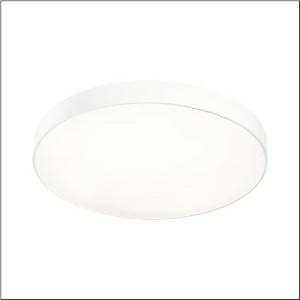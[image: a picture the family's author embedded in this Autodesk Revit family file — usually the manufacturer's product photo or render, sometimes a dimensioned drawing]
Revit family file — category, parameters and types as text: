
# Revit family: round_21_l_51mr38fd0421w
name_source: partatom
category: Lighting Fixtures
units: mm (PartAtom-declared; Revit-internal decimal feet)

## family parameters
Cut with Voids When Loaded = No
Host = Face
Light Source = No
Part Type = Normal
Room Calculation Point = No
Round Connector Dimension = Use Diameter
Shared = No

## types (1)
- Round 21 L (1 x LED, 14150 lm, 97 W, 4000K)
    Apparent Load = 97 VA
    CIE Flux Codes = 49 80 96 100 100
    Color Rendering = 80
    Color Temperature = 4000K
    Default Elevation = 1800 mm
    Description = Round 21 L, wall and ceiling luminaire, primary optical cover: cover, of PMMA, opal, light emission: direct distribution, primary light characteristic: symmetric, installation type: suspended mounting, surface-mounted, LED, rated luminous flux: 13.080lm, luminous efficacy: 146lm/W, light colour: 840, colour temperature: 4000K, control gear: DALI 2, with terminal, 5-pole, mains connection: 230V, AC, 50/60Hz, rated input power: 97W, housing, of aluminium, coated, white, diameter: 850mm, height: 62mm, protection rating (complete): IP40, insulation class (complete): insulation class I (protective earthing), certification: CE, impact resistance: IK04, permissible operating ambient temperature: -10..+35°C, packaging unit: 1 piece
    Height = 87 mm
    Lamp = 1 x LED
    Lamp Light Flux = 14150 lm
    Lamp Power = 97 W
    Lamp count = 1
    Length = 850 mm
    Luminous efficacy = 146 lm/W
    Manufacturer = Siteco
    ModVariant = No
    Model = 51MR38FD0421W
    Mounting Place = Ceiling
    Mounting Type = Surface mounted
    Number of Poles = 1
    OnlyDefault = Yes
    Power Factor = 1
    Product Name = Round 21 L
    Product group = wall and ceiling luminaire | ceiling mounted
    ProductGroupID = 304
    Protection Class = Protection class I
    Protection Degree = IP 40
    RLX_Detail_Level = 1
    RLX_Emergency_Light_Flux = 0 lm
    RLX_Emergency_Type = 0
    RLX_Emergency_Type_DB = No
    RlxData = <blob elided: 15025 chars, md5=9272d121>
    Socket = socket
    Standby Power = 0 W
    System Light Flux = 14150 lm
    System Power = 97 W
    Type Comments = Product without accessories
    Type Image = l_1258320.jpg
    URL = http://relux.com
    VarID = ---
    Voltage = 0 V
    Weight = 0.00 kg
    Width = 0 mm  [stored 0 ft]

note: [stored X ft] marks values corroborated as IEEE doubles in the binary element streams (Revit-internal decimal feet)

## geometry (parser evidence)
native form markers: Sweep x12
no freeform markers — native parametric forms only
